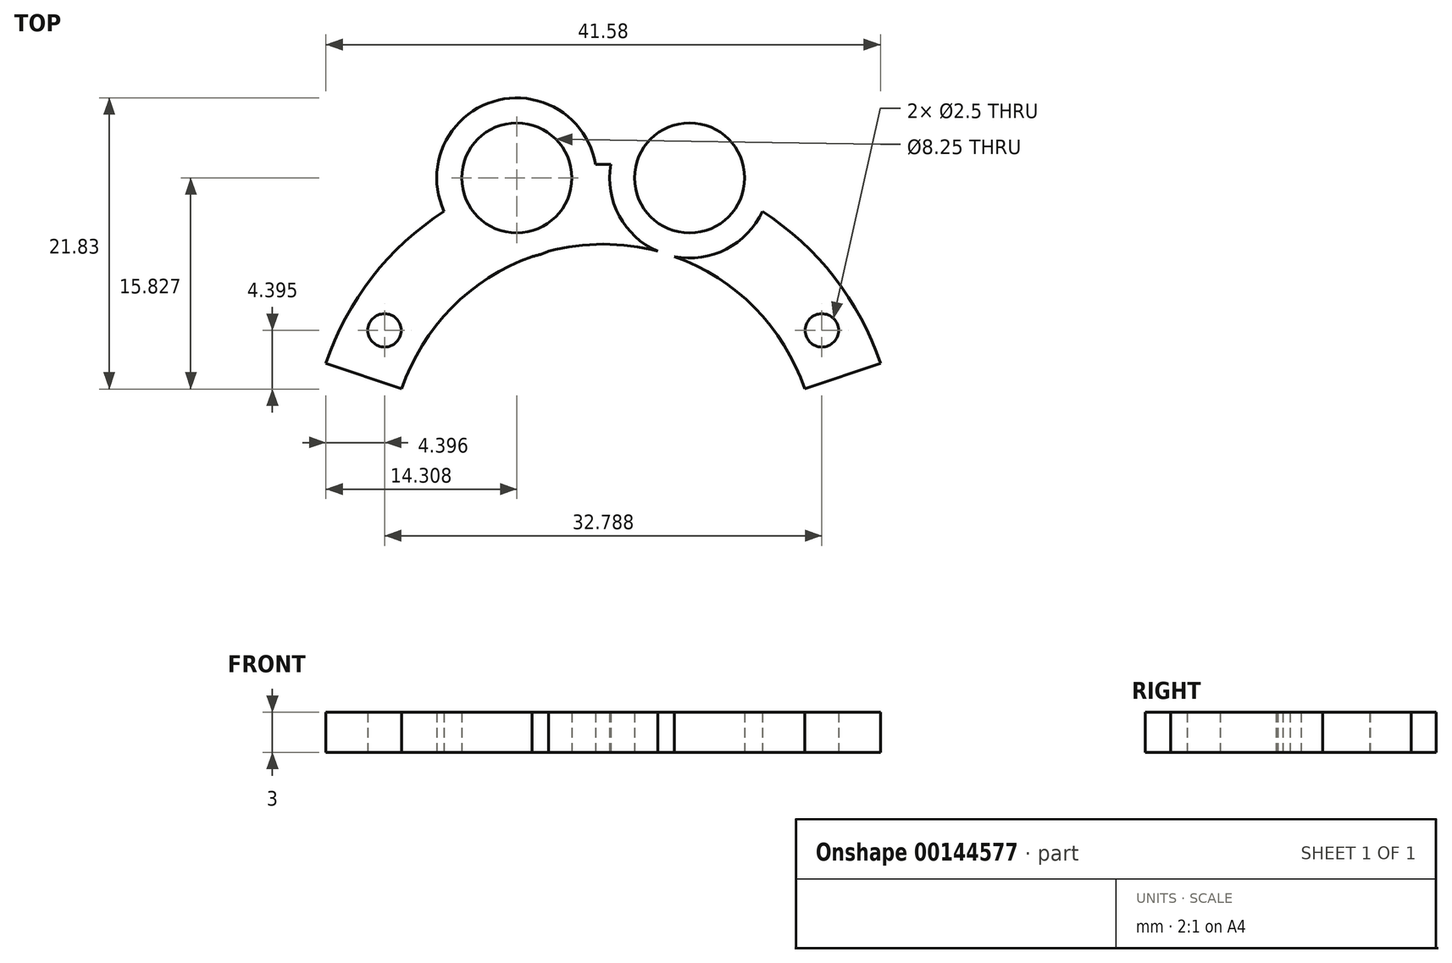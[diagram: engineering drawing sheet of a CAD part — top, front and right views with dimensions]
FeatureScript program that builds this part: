
annotation { "Feature Type Name" : "Feature", "Feature Type Description" : "" }
export const myFeature = defineFeature(function(context is Context, id is Id, definition is map)
    precondition{}
    {
        {
            var Q0;
            Q0=qCreatedBy(makeId("Top.planeOp"),FACE);
            var sketch = newSketch(context, id + "F0", { "sketchPlane" : qUnion([Q0])});
            skCircle(sketch, "E0", {"center": v(0, 0) * mm, "radius": 23.68 * mm, "construction": true});
            skCircle(sketch, "E1", {"center": v(-16.4, 9.46) * mm, "radius": 1.25 * mm});
            skCircle(sketch, "E2", {"center": v(16.4, 9.47) * mm, "radius": 1.25 * mm});
            skLineSegment(sketch, "E3", {"start": v(16.4, 9.47) * mm, "end": v(0, 0) * mm, "construction": true});
            skLineSegment(sketch, "E4", {"start": v(-16.4, 9.46) * mm, "end": v(0, 0) * mm, "construction": true});
            skCircle(sketch, "E5", {"center": v(0, 0) * mm, "radius": 8 * mm, "construction": true});
            skLineSegment(sketch, "E6", {"start": v(-23.68, 0) * mm, "end": v(23.68, 0) * mm});
            skCircle(sketch, "E7", {"center": v(0, 0) * mm, "radius": 15.93 * mm});
            skCircle(sketch, "E8", {"center": v(0, 0) * mm, "radius": 21.93 * mm});
            skLineSegment(sketch, "E9", {"start": v(0, 0) * mm, "end": v(-22.45, 7.54) * mm});
            skLineSegment(sketch, "E10.MirrorCS", {"start": v(0, 0) * mm, "end": v(22.45, 7.54) * mm});
            skPoint(sketch, "E11", {"position": v(-20.79, 6.99) * mm});
            skPoint(sketch, "E12", {"position": v(-15.1, 5.07) * mm});
            skPoint(sketch, "E13", {"position": v(15.1, 5.07) * mm});
            skPoint(sketch, "E14", {"position": v(20.79, 6.99) * mm});
            skSolve(sketch);
        }
        {
            var Q0;
            Q0=makeQuery(id+"F0.imprint","IMPRINT",FACE,{"disambiguationData":[TD([[makeQuery(id+"F0.imprint","IMPRINT",EDGE,{"derivedFrom":sQuery(id+"F0.wireOp",EDGE,"E1")}),-1.0]])]});
            extrude(context, id + "F1", {"entities" : qUnion([Q0]), "depth" : 3 * mm});
        }
        {
            var Q0;
            Q0=qCreatedBy(makeId("Top.planeOp"),FACE);
            var sketch = newSketch(context, id + "F2", { "sketchPlane" : qUnion([Q0])});
            skCircle(sketch, "E15", {"center": v(-6.48, 20.9) * mm, "radius": 6 * mm});
            skCircle(sketch, "E16", {"center": v(-6.48, 20.9) * mm, "radius": 4.12 * mm});
            skCircle(sketch, "E17.MirrorC", {"center": v(6.48, 20.9) * mm, "radius": 4.12 * mm});
            skCircle(sketch, "E18.MirrorC", {"center": v(6.48, 20.9) * mm, "radius": 6 * mm});
            skSolve(sketch);
        }
        {
            var Q0;
            Q0=makeQuery(id+"F2.imprint","IMPRINT",FACE,{"disambiguationData":[TD([[makeQuery(id+"F2.imprint","IMPRINT",EDGE,{"derivedFrom":sQuery(id+"F2.wireOp",EDGE,"E17.MirrorC")}),1.0]])]});
            var Q1;
            Q1=makeQuery(id+"F2.imprint","IMPRINT",FACE,{"disambiguationData":[TD([[makeQuery(id+"F2.imprint","IMPRINT",EDGE,{"derivedFrom":sQuery(id+"F2.wireOp",EDGE,"E15")}),1.0]])]});
            extrude(context, id + "F3", {"entities" : qUnion([Q0, Q1]), "operationType" : NewBodyOperationType.ADD, "depth" : 3 * mm});
        }
        {
            var Q0;
            Q0=makeQuery(id+"F2.imprint","IMPRINT",FACE,{"disambiguationData":[TD([[makeQuery(id+"F2.imprint","IMPRINT",EDGE,{"derivedFrom":sQuery(id+"F2.wireOp",EDGE,"E16")}),1.0]])]});
            var Q1;
            Q1=makeQuery(id+"F2.imprint","IMPRINT",FACE,{"disambiguationData":[TD([[makeQuery(id+"F2.imprint","IMPRINT",EDGE,{"derivedFrom":sQuery(id+"F2.wireOp",EDGE,"E17.MirrorC")}),-1.0]])]});
            extrude(context, id + "F4", {"entities" : qUnion([Q0, Q1]), "operationType" : NewBodyOperationType.REMOVE, "depth" : 13.64 * mm});
        }
    });
